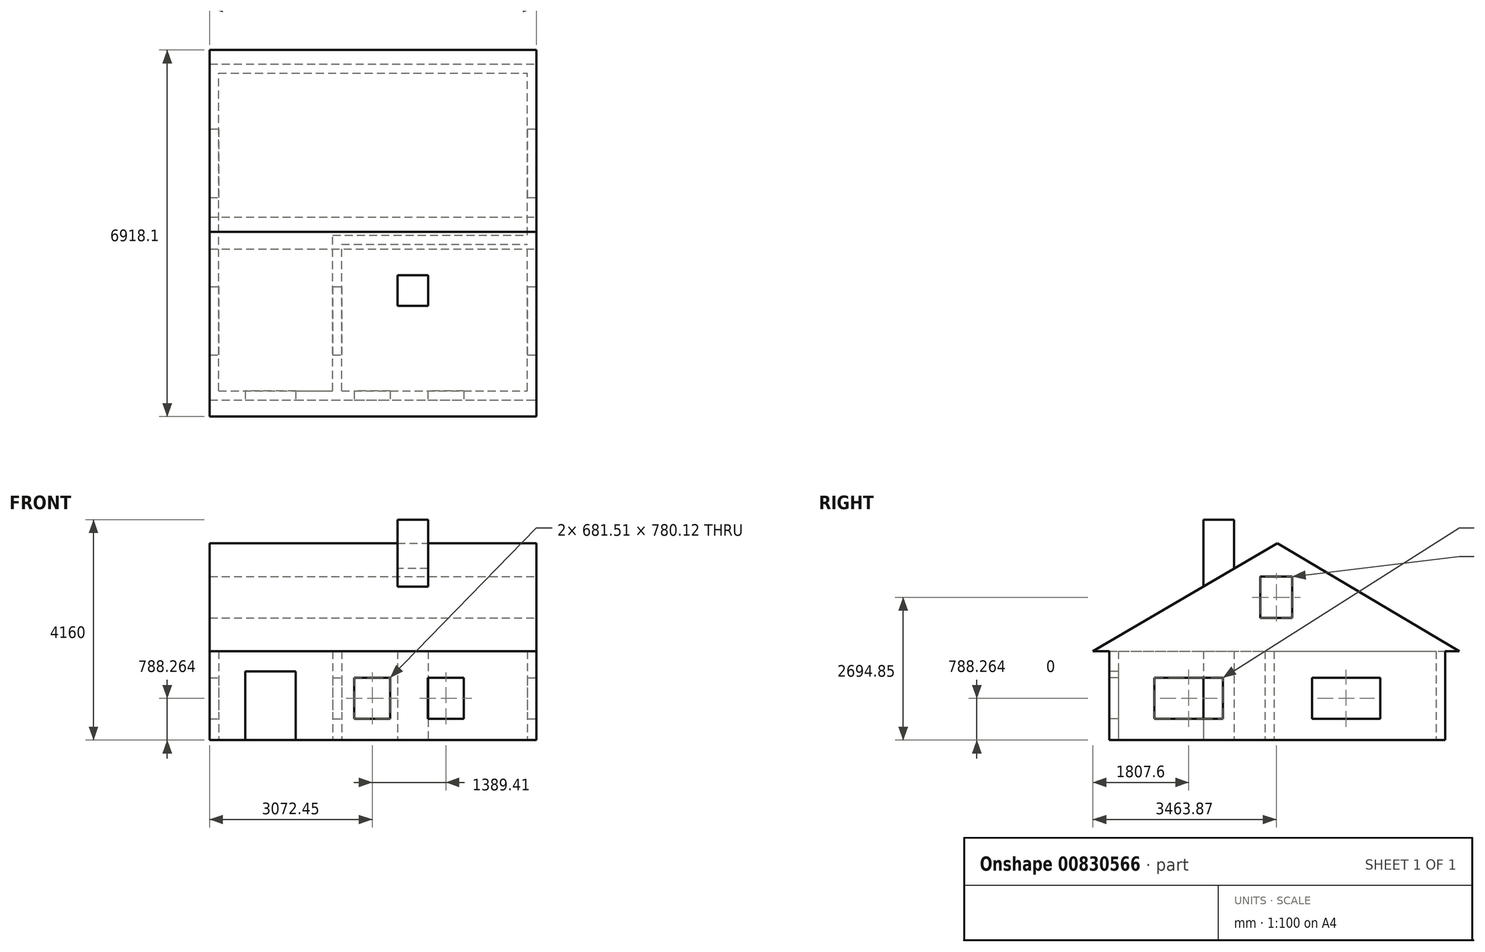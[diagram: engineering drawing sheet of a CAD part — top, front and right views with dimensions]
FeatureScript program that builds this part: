
annotation { "Feature Type Name" : "Feature", "Feature Type Description" : "" }
export const myFeature = defineFeature(function(context is Context, id is Id, definition is map)
    precondition{}
    {
        {
            var Q0;
            Q0=qCreatedBy(makeId("Top.planeOp"),FACE);
            var sketch = newSketch(context, id + "F0", { "sketchPlane" : qUnion([Q0])});
            skLineSegment(sketch, "E0.bottom", {"start": v(0, 0) * mm, "end": v(5831.56, 0) * mm});
            skLineSegment(sketch, "E0.top", {"start": v(0, 6000) * mm, "end": v(5831.56, 6000) * mm});
            skLineSegment(sketch, "E0.left", {"start": v(0, 0) * mm, "end": v(0, 6000) * mm});
            skLineSegment(sketch, "E0.right", {"start": v(5831.56, 0) * mm, "end": v(5831.56, 6000) * mm});
            skLineSegment(sketch, "E1.0", {"start": v(-170, -170) * mm, "end": v(-170, 6170) * mm});
            skLineSegment(sketch, "E1.1", {"start": v(-170, -170) * mm, "end": v(6001.56, -170) * mm});
            skLineSegment(sketch, "E1.2", {"start": v(6001.56, -170) * mm, "end": v(6001.56, 6170) * mm});
            skLineSegment(sketch, "E1.3", {"start": v(-170, 6170) * mm, "end": v(6001.56, 6170) * mm});
            skLineSegment(sketch, "E2.bottom", {"start": v(2324.12, 0) * mm, "end": v(5831.56, 0) * mm});
            skLineSegment(sketch, "E2.top", {"start": v(2324.12, 2768.97) * mm, "end": v(5831.56, 2768.97) * mm});
            skLineSegment(sketch, "E2.left", {"start": v(2324.12, 0) * mm, "end": v(2324.12, 2768.97) * mm});
            skLineSegment(sketch, "E2.right", {"start": v(5831.56, 0) * mm, "end": v(5831.56, 2768.97) * mm});
            skLineSegment(sketch, "E3.0", {"start": v(2154.12, 2938.97) * mm, "end": v(5831.56, 2938.97) * mm});
            skLineSegment(sketch, "E3.1", {"start": v(2154.12, 0) * mm, "end": v(2154.12, 2938.97) * mm});
            skSolve(sketch);
        }
        {
            var Q0;
            Q0 = qSketchRegion(id + "F0", true);
            var Q1;
            {var subQ3=sQuery(id+"F0.wireOp",EDGE,"E2.top");Q1=makeQuery(id+"F0.imprint","IMPRINT",FACE,{"disambiguationData":[TD([[makeQuery(id+"F0.imprint","IMPRINT",EDGE,{"derivedFrom":subQ3}),1.0]])]});}
            extrude(context, id + "F1", {"entities" : qUnion([Q0, Q1]), "depth" : 1680 * mm, "offsetDistance" : 25 * mm});
        }
        {
            var Q0;
            Q0=makeQuery(id+"F1.opExtrude","SWEPT_FACE",FACE,{"disambiguationData":[OSD([sQuery(id+"F0.wireOp",EDGE,"E1.1")])]});
            var sketch = newSketch(context, id + "F2", { "sketchPlane" : qUnion([Q0])});
            skLineSegment(sketch, "E4.bottom", {"start": v(505.88, 0) * mm, "end": v(1458.45, 0) * mm});
            skLineSegment(sketch, "E4.top", {"start": v(505.88, 1298.45) * mm, "end": v(1458.45, 1298.45) * mm});
            skLineSegment(sketch, "E4.left", {"start": v(505.88, 0) * mm, "end": v(505.88, 1298.45) * mm});
            skLineSegment(sketch, "E4.right", {"start": v(1458.45, 0) * mm, "end": v(1458.45, 1298.45) * mm});
            skLineSegment(sketch, "E5.bottom", {"start": v(2561.69, 398.2) * mm, "end": v(3243.2, 398.2) * mm});
            skLineSegment(sketch, "E5.top", {"start": v(2561.69, 1178.33) * mm, "end": v(3243.2, 1178.33) * mm});
            skLineSegment(sketch, "E5.left", {"start": v(2561.69, 398.2) * mm, "end": v(2561.69, 1178.33) * mm});
            skLineSegment(sketch, "E5.right", {"start": v(3243.2, 398.2) * mm, "end": v(3243.2, 1178.33) * mm});
            skLineSegment(sketch, "E6.bottom", {"start": v(3951.1, 398.2) * mm, "end": v(4632.62, 398.2) * mm});
            skLineSegment(sketch, "E6.top", {"start": v(3951.1, 1178.33) * mm, "end": v(4632.62, 1178.33) * mm});
            skLineSegment(sketch, "E6.left", {"start": v(3951.1, 398.2) * mm, "end": v(3951.1, 1178.33) * mm});
            skLineSegment(sketch, "E6.right", {"start": v(4632.62, 398.2) * mm, "end": v(4632.62, 1178.33) * mm});
            skSolve(sketch);
        }
        {
            var Q0;
            Q0 = qSketchRegion(id + "F2", true);
            extrude(context, id + "F3", {"entities" : qUnion([Q0]), "operationType" : NewBodyOperationType.REMOVE, "oppositeDirection" : true, "depth" : 1140 * mm, "offsetDistance" : 25 * mm});
        }
        {
            var Q0;
            Q0=makeQuery(id+"F1.opExtrude","SWEPT_FACE",FACE,{"disambiguationData":[OSD([sQuery(id+"F0.wireOp",EDGE,"E1.2")])]});
            var sketch = newSketch(context, id + "F4", { "sketchPlane" : qUnion([Q0])});
            skLineSegment(sketch, "E7", {"start": v(-482.79, 1680) * mm, "end": v(6435.31, 1680) * mm});
            skLineSegment(sketch, "E8", {"start": v(6435.31, 1680) * mm, "end": v(3000, 3716.67) * mm});
            skLineSegment(sketch, "E9", {"start": v(3000, 3716.67) * mm, "end": v(-482.79, 1680) * mm});
            skPoint(sketch, "E10", {"position": v(-170, 1680) * mm});
            skPoint(sketch, "E11", {"position": v(6170, 1680) * mm});
            skSolve(sketch);
        }
        {
            var Q0;
            Q0 = qSketchRegion(id + "F4", true);
            extrude(context, id + "F5", {"entities" : qUnion([Q0]), "operationType" : NewBodyOperationType.ADD, "oppositeDirection" : true, "depth" : 6170 * mm, "offsetDistance" : 25 * mm});
        }
        {
            var Q0;
            Q0=makeQuery(id+"F5.boolean.opBoolean","MERGE",FACE,{"derivedFrom":[makeQuery(id+"F1.opExtrude","SWEPT_FACE",FACE,{"disambiguationData":[OSD([sQuery(id+"F0.wireOp",EDGE,"E1.2")])]}),makeQuery(id+"F5.opExtrude","CAP_FACE",FACE,{"disambiguationData":[OSD([sQuery(id+"F4.wireOp",EDGE,"E7"),sQuery(id+"F4.wireOp",EDGE,"E8"),sQuery(id+"F4.wireOp",EDGE,"E9")])],"isStart":true})]});
            var sketch = newSketch(context, id + "F6", { "sketchPlane" : qUnion([Q0])});
            skLineSegment(sketch, "E12.bottom", {"start": v(679.41, 398.2) * mm, "end": v(1970.2, 398.2) * mm});
            skLineSegment(sketch, "E12.top", {"start": v(679.41, 1178.33) * mm, "end": v(1970.2, 1178.33) * mm});
            skLineSegment(sketch, "E12.left", {"start": v(679.41, 398.2) * mm, "end": v(679.41, 1178.33) * mm});
            skLineSegment(sketch, "E12.right", {"start": v(1970.2, 398.2) * mm, "end": v(1970.2, 1178.33) * mm});
            skLineSegment(sketch, "E13.bottom", {"start": v(3653.02, 398.2) * mm, "end": v(4943.8, 398.2) * mm});
            skLineSegment(sketch, "E13.top", {"start": v(3653.02, 1178.33) * mm, "end": v(4943.8, 1178.33) * mm});
            skLineSegment(sketch, "E13.left", {"start": v(3653.02, 398.2) * mm, "end": v(3653.02, 1178.33) * mm});
            skLineSegment(sketch, "E13.right", {"start": v(4943.8, 398.2) * mm, "end": v(4943.8, 1178.33) * mm});
            skLineSegment(sketch, "E14.bottom", {"start": v(2678.47, 3084.9) * mm, "end": v(3283.68, 3084.9) * mm});
            skLineSegment(sketch, "E14.top", {"start": v(2678.47, 2304.79) * mm, "end": v(3283.68, 2304.79) * mm});
            skLineSegment(sketch, "E14.left", {"start": v(2678.47, 3084.9) * mm, "end": v(2678.47, 2304.79) * mm});
            skLineSegment(sketch, "E14.right", {"start": v(3283.68, 3084.9) * mm, "end": v(3283.68, 2304.79) * mm});
            skSolve(sketch);
        }
        {
            var Q0;
            Q0 = qSketchRegion(id + "F6", true);
            extrude(context, id + "F7", {"entities" : qUnion([Q0]), "operationType" : NewBodyOperationType.REMOVE, "oppositeDirection" : true, "depth" : 7440 * mm, "offsetDistance" : 25 * mm});
        }
        {
            var Q0;
            Q0=qCreatedBy(makeId("Top.planeOp"),FACE);
            var sketch = newSketch(context, id + "F8", { "sketchPlane" : qUnion([Q0])});
            skLineSegment(sketch, "E15.bottom", {"start": v(3377.88, 1602.93) * mm, "end": v(3956.58, 1602.93) * mm});
            skLineSegment(sketch, "E15.top", {"start": v(3377.88, 2181.63) * mm, "end": v(3956.58, 2181.63) * mm});
            skLineSegment(sketch, "E15.left", {"start": v(3377.88, 1602.93) * mm, "end": v(3377.88, 2181.63) * mm});
            skLineSegment(sketch, "E15.right", {"start": v(3956.58, 1602.93) * mm, "end": v(3956.58, 2181.63) * mm});
            skSolve(sketch);
        }
        {
            var Q0;
            Q0 = qSketchRegion(id + "F8", true);
            extrude(context, id + "F9", {"entities" : qUnion([Q0]), "operationType" : NewBodyOperationType.ADD, "depth" : 4160 * mm, "offsetDistance" : 25 * mm});
        }
    });
